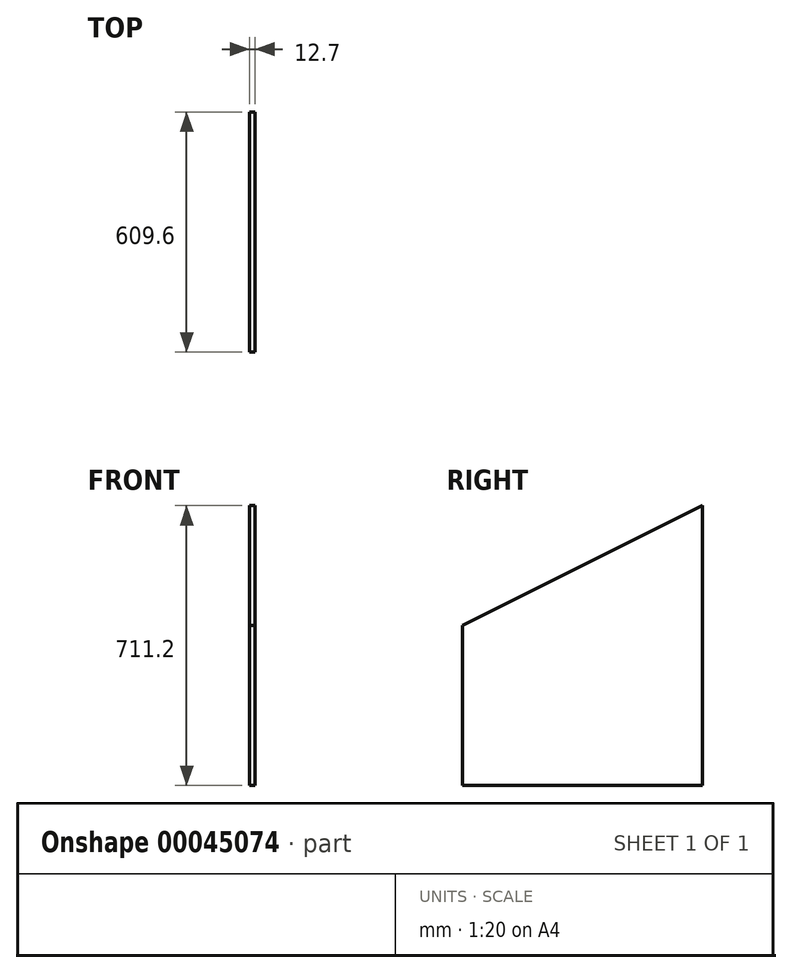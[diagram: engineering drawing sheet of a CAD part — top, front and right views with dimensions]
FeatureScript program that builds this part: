
annotation { "Feature Type Name" : "Feature", "Feature Type Description" : "" }
export const myFeature = defineFeature(function(context is Context, id is Id, definition is map)
    precondition{}
    {
        {
            var Q0;
            Q0=qCreatedBy(makeId("Right.planeOp"),FACE);
            var sketch = newSketch(context, id + "F0", { "sketchPlane" : qUnion([Q0])});
            skLineSegment(sketch, "E0.rect.top", {"start": v(304.8, -406.4) * mm, "end": v(-304.8, -406.4) * mm});
            skLineSegment(sketch, "E0.rect.left", {"start": v(304.8, 304.8) * mm, "end": v(304.8, -406.4) * mm});
            skLineSegment(sketch, "E0.rect.right", {"start": v(-304.8, 0) * mm, "end": v(-304.8, -406.4) * mm});
            skPoint(sketch, "E0.rect.middle", {"position": v(0, 0) * mm});
            skLineSegment(sketch, "E1", {"start": v(-304.8, 0) * mm, "end": v(304.8, 304.8) * mm});
            skSolve(sketch);
        }
        {
            var Q0;
            Q0=makeQuery(id+"F0.imprint","IMPRINT",FACE,{"disambiguationData":[TD([[makeQuery(id+"F0.imprint","IMPRINT",EDGE,{"derivedFrom":sQuery(id+"F0.wireOp",EDGE,"E0.rect.top")}),-1.0]])]});
            extrude(context, id + "F1", {"entities" : qUnion([Q0]), "depth" : 12.7 * mm});
        }
    });
